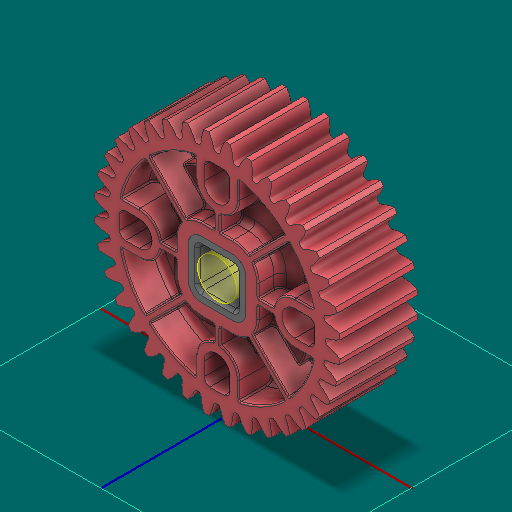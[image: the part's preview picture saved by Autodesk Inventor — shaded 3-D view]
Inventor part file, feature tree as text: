
AUTODESK INVENTOR PART (.ipt)
format: ipt  version: 2025 (Build 290162000, 162)  size: 3,367,424 bytes
history: native  units: in
note: dims shown in document units (in); Inventor stores cm internally (conversion verified against a paired STEP export)
features: other x6, sketch x1
ambient origin geometry x8: Origin, YZ Plane, XZ Plane, XY Plane, X Axis, Y Axis, Z Axis, Center Point
bodies: Solid1 (feature_tree), Solid2 (feature_tree)
feature tree (7):
  other  "HS 36T Gear, No Insert.ipt"
  other  "Solid1::HS 36T Gear, No Insert.ipt"
  other  "Solid2::HS 36T Gear, No Insert.ipt"
  other  "TaggingFeature1"
  sketch  "Sketch1"  dims[d0=0.3937in]
  other  "Srf1"
  other  "Srf1::Derived"
